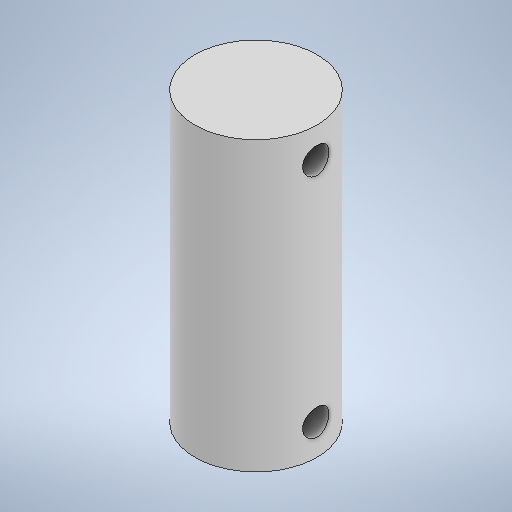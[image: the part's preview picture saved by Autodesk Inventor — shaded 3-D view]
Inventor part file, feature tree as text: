
AUTODESK INVENTOR PART (.ipt)
format: ipt  version: 2025 (Build 290162010, 162A)  size: 235,520 bytes
history: native  units: in
note: dims shown in document units (in); Inventor stores cm internally (conversion verified against a paired STEP export)
features: sketch x2, extrude x1, plane x1, hole x1
ambient origin geometry x8: Origin, YZ Plane, XZ Plane, XY Plane, X Axis, Y Axis, Z Axis, Center Point
bodies: Solid1 (feature_tree)
feature tree (5):
  extrude  "Extrusion1"  Depth=1.2992in TaperAngle=0.0deg
  plane  "Work Plane1"
  hole  "Hole1"  [1 undecoded]
  sketch  "Sketch1"  dims[d0=0.5512in d1=1.2992in d2=0.0in]
  sketch  "Sketch2"  dims[d3=0.2756in d4=0.1378in d5=0.1378in d6=0.1181in d7=0.2362in d8=0.1575in d9=0.0787in d10=90.0deg d11=1.378in d12=0.0in]
note: 1 required parameter value undecoded (feature->parameter linkage not recoverable at this tier; creation-order binding heuristic only, values carry confidence <= 0.55)
